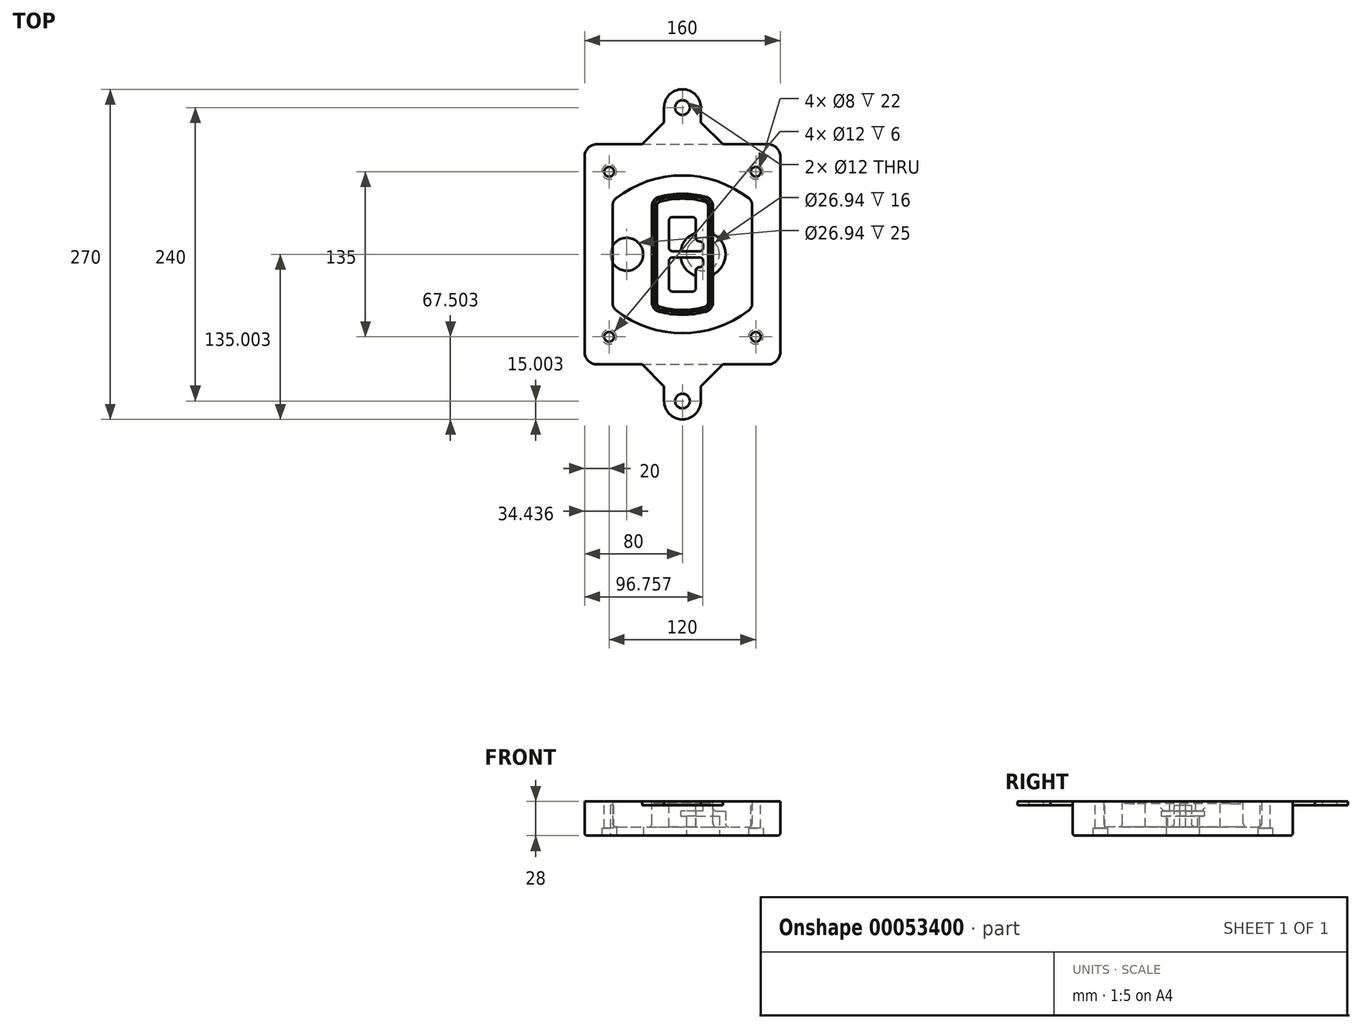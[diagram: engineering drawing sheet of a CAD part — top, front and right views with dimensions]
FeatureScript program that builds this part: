
annotation { "Feature Type Name" : "Feature", "Feature Type Description" : "" }
export const myFeature = defineFeature(function(context is Context, id is Id, definition is map)
    precondition{}
    {
        {
            var Q0;
            Q0=qCreatedBy(makeId("Top.planeOp"),FACE);
            var sketch = newSketch(context, id + "F0", { "sketchPlane" : qUnion([Q0])});
            skPoint(sketch, "E0.rect.middle", {"position": v(0, 0) * mm});
            skLineSegment(sketch, "E1.bottom", {"start": v(24.05, 28.38) * mm, "end": v(164.05, 28.38) * mm});
            skLineSegment(sketch, "E1.top", {"start": v(24.05, 208.38) * mm, "end": v(164.05, 208.38) * mm});
            skLineSegment(sketch, "E1.left", {"start": v(14.05, 38.38) * mm, "end": v(14.05, 198.38) * mm});
            skLineSegment(sketch, "E1.right", {"start": v(174.05, 38.38) * mm, "end": v(174.05, 198.38) * mm});
            skLineSegment(sketch, "E2", {"start": v(14.05, 208.38) * mm, "end": v(174.05, 28.38) * mm, "construction": true});
            skLineSegment(sketch, "E3", {"start": v(174.05, 208.38) * mm, "end": v(14.05, 28.38) * mm, "construction": true});
            skCircle(sketch, "E4", {"center": v(34.05, 185.88) * mm, "radius": 4 * mm});
            skCircle(sketch, "E5", {"center": v(154.05, 185.88) * mm, "radius": 4 * mm});
            skCircle(sketch, "E6", {"center": v(154.05, 50.88) * mm, "radius": 4 * mm});
            skCircle(sketch, "E7", {"center": v(34.05, 50.88) * mm, "radius": 4 * mm});
            skLineSegment(sketch, "E8", {"start": v(34.05, 185.88) * mm, "end": v(154.05, 185.88) * mm, "construction": true});
            skLineSegment(sketch, "E9", {"start": v(154.05, 185.88) * mm, "end": v(154.05, 50.88) * mm, "construction": true});
            skLineSegment(sketch, "E10", {"start": v(154.05, 50.88) * mm, "end": v(34.05, 50.88) * mm, "construction": true});
            skLineSegment(sketch, "E11", {"start": v(34.05, 50.88) * mm, "end": v(34.05, 185.88) * mm, "construction": true});
            skLineSegment(sketch, "E12", {"start": v(34.05, 158.68) * mm, "end": v(34.05, 78.09) * mm});
            skLineSegment(sketch, "E13", {"start": v(154.05, 158.68) * mm, "end": v(154.05, 78.09) * mm});
            skArc(sketch, "E14", {"start": v(150.2, 166.56) * mm, "mid": v(94.05, 185.88) * mm, "end": v(37.9, 166.56) * mm});
            skArc(sketch, "E15", {"start": v(37.9, 70.2) * mm, "mid": v(94.05, 50.88) * mm, "end": v(150.2, 70.2) * mm});
            skLineSegment(sketch, "E16", {"start": v(34.05, 118.38) * mm, "end": v(154.05, 118.38) * mm, "construction": true});
            skPoint(sketch, "E17.visualSharp", {"position": v(34.05, 73.38) * mm});
            skArc(sketch, "E17.filletArc", {"start": v(34.05, 78.09) * mm, "mid": v(35.06, 73.7) * mm, "end": v(37.9, 70.2) * mm});
            skPoint(sketch, "E18.visualSharp", {"position": v(34.05, 163.38) * mm});
            skArc(sketch, "E18.filletArc", {"start": v(37.9, 166.56) * mm, "mid": v(35.06, 163.06) * mm, "end": v(34.05, 158.68) * mm});
            skPoint(sketch, "E19.visualSharp", {"position": v(154.05, 163.38) * mm});
            skArc(sketch, "E19.filletArc", {"start": v(154.05, 158.68) * mm, "mid": v(153.04, 163.06) * mm, "end": v(150.2, 166.56) * mm});
            skPoint(sketch, "E20.visualSharp", {"position": v(154.05, 73.38) * mm});
            skArc(sketch, "E20.filletArc", {"start": v(150.2, 70.2) * mm, "mid": v(153.04, 73.7) * mm, "end": v(154.05, 78.09) * mm});
            skPoint(sketch, "E21.visualSharp", {"position": v(14.05, 208.38) * mm});
            skArc(sketch, "E21.filletArc", {"start": v(24.05, 208.38) * mm, "mid": v(16.98, 205.45) * mm, "end": v(14.05, 198.38) * mm});
            skPoint(sketch, "E22.visualSharp", {"position": v(174.05, 208.38) * mm});
            skArc(sketch, "E22.filletArc", {"start": v(174.05, 198.38) * mm, "mid": v(171.12, 205.45) * mm, "end": v(164.05, 208.38) * mm});
            skPoint(sketch, "E23.visualSharp", {"position": v(174.05, 28.38) * mm});
            skArc(sketch, "E23.filletArc", {"start": v(164.05, 28.38) * mm, "mid": v(171.12, 31.31) * mm, "end": v(174.05, 38.38) * mm});
            skPoint(sketch, "E24.visualSharp", {"position": v(14.05, 28.38) * mm});
            skArc(sketch, "E24.filletArc", {"start": v(14.05, 38.38) * mm, "mid": v(16.98, 31.31) * mm, "end": v(24.05, 28.38) * mm});
            skArc(sketch, "E25.0", {"start": v(151.05, 158.68) * mm, "mid": v(150.34, 161.75) * mm, "end": v(148.36, 164.2) * mm});
            skLineSegment(sketch, "E25.1", {"start": v(151.05, 158.68) * mm, "end": v(151.05, 78.09) * mm});
            skArc(sketch, "E25.2", {"start": v(148.36, 72.57) * mm, "mid": v(150.34, 75.02) * mm, "end": v(151.05, 78.09) * mm});
            skArc(sketch, "E25.3", {"start": v(39.74, 72.57) * mm, "mid": v(94.05, 53.88) * mm, "end": v(148.36, 72.57) * mm});
            skArc(sketch, "E25.4", {"start": v(37.05, 78.09) * mm, "mid": v(37.76, 75.02) * mm, "end": v(39.74, 72.57) * mm});
            skArc(sketch, "E25.5", {"start": v(148.36, 164.2) * mm, "mid": v(94.05, 182.88) * mm, "end": v(39.74, 164.2) * mm});
            skLineSegment(sketch, "E25.6", {"start": v(37.05, 158.68) * mm, "end": v(37.05, 78.09) * mm});
            skArc(sketch, "E25.7", {"start": v(39.74, 164.2) * mm, "mid": v(37.76, 161.75) * mm, "end": v(37.05, 158.68) * mm});
            skArc(sketch, "E26.0", {"start": v(35.43, 169.71) * mm, "mid": v(31.47, 164.82) * mm, "end": v(30.05, 158.68) * mm});
            skArc(sketch, "E26.1", {"start": v(152.67, 169.71) * mm, "mid": v(94.05, 189.88) * mm, "end": v(35.43, 169.71) * mm});
            skArc(sketch, "E26.2", {"start": v(158.05, 158.68) * mm, "mid": v(156.63, 164.82) * mm, "end": v(152.67, 169.71) * mm});
            skLineSegment(sketch, "E26.3", {"start": v(158.05, 158.68) * mm, "end": v(158.05, 78.09) * mm});
            skArc(sketch, "E26.4", {"start": v(152.67, 67.05) * mm, "mid": v(156.63, 71.95) * mm, "end": v(158.05, 78.09) * mm});
            skLineSegment(sketch, "E26.5", {"start": v(30.05, 158.68) * mm, "end": v(30.05, 78.09) * mm});
            skArc(sketch, "E26.6", {"start": v(35.43, 67.05) * mm, "mid": v(94.05, 46.88) * mm, "end": v(152.67, 67.05) * mm});
            skArc(sketch, "E26.7", {"start": v(30.05, 78.09) * mm, "mid": v(31.47, 71.95) * mm, "end": v(35.43, 67.05) * mm});
            skSolve(sketch);
        }
        {
            var Q0;
            Q0=makeQuery(id+"F0.imprint","IMPRINT",FACE,{"disambiguationData":[TD([[makeQuery(id+"F0.imprint","IMPRINT",EDGE,{"derivedFrom":sQuery(id+"F0.wireOp",EDGE,"E1.bottom")}),1.0]])]});
            var Q1;
            Q1=makeQuery(id+"F0.imprint","IMPRINT",FACE,{"disambiguationData":[TD([[makeQuery(id+"F0.imprint","IMPRINT",EDGE,{"derivedFrom":sQuery(id+"F0.wireOp",EDGE,"E12")}),1.0]])]});
            var Q2;
            Q2=makeQuery(id+"F0.imprint","IMPRINT",FACE,{"disambiguationData":[TD([[makeQuery(id+"F0.imprint","IMPRINT",EDGE,{"derivedFrom":sQuery(id+"F0.wireOp",EDGE,"E25.0")}),1.0]])]});
            var Q3;
            Q3=makeQuery(id+"F0.imprint","IMPRINT",FACE,{"disambiguationData":[TD([[makeQuery(id+"F0.imprint","IMPRINT",EDGE,{"derivedFrom":sQuery(id+"F0.wireOp",EDGE,"E12")}),-1.0]])]});
            extrude(context, id + "F1", {"entities" : qUnion([Q0, Q1, Q2, Q3]), "oppositeDirection" : true, "depth" : 25 * mm});
        }
        {
            var Q0;
            Q0=makeQuery(id+"F0.imprint","IMPRINT",FACE,{"disambiguationData":[TD([[makeQuery(id+"F0.imprint","IMPRINT",EDGE,{"derivedFrom":sQuery(id+"F0.wireOp",EDGE,"E12")}),1.0]])]});
            extrude(context, id + "F2", {"entities" : qUnion([Q0]), "operationType" : NewBodyOperationType.ADD, "depth" : 3 * mm});
        }
        {
            var Q0;
            Q0=makeQuery(id+"F0.imprint","IMPRINT",FACE,{"disambiguationData":[TD([[makeQuery(id+"F0.imprint","IMPRINT",EDGE,{"derivedFrom":sQuery(id+"F0.wireOp",EDGE,"E25.0")}),1.0]])]});
            extrude(context, id + "F3", {"entities" : qUnion([Q0]), "operationType" : NewBodyOperationType.REMOVE, "oppositeDirection" : true, "depth" : 18 * mm});
        }
        {
            var Q0;
            Q0=makeQuery(id+"F2.opExtrude","CAP_FACE",FACE,{"disambiguationData":[OSD([sQuery(id+"F0.wireOp",EDGE,"E12"),sQuery(id+"F0.wireOp",EDGE,"E13"),sQuery(id+"F0.wireOp",EDGE,"E14"),sQuery(id+"F0.wireOp",EDGE,"E15"),sQuery(id+"F0.wireOp",EDGE,"E17.filletArc"),sQuery(id+"F0.wireOp",EDGE,"E18.filletArc"),sQuery(id+"F0.wireOp",EDGE,"E19.filletArc"),sQuery(id+"F0.wireOp",EDGE,"E20.filletArc"),sQuery(id+"F0.wireOp",EDGE,"E25.0"),sQuery(id+"F0.wireOp",EDGE,"E25.1"),sQuery(id+"F0.wireOp",EDGE,"E25.2"),sQuery(id+"F0.wireOp",EDGE,"E25.3"),sQuery(id+"F0.wireOp",EDGE,"E25.4"),sQuery(id+"F0.wireOp",EDGE,"E25.5"),sQuery(id+"F0.wireOp",EDGE,"E25.6"),sQuery(id+"F0.wireOp",EDGE,"E25.7")])],"isStart":false});
            var sketch = newSketch(context, id + "F4", { "sketchPlane" : qUnion([Q0])});
            skArc(sketch, "E27.0", {"start": v(74.97, 71.41) * mm, "mid": v(94.05, 68.88) * mm, "end": v(113.13, 71.41) * mm});
            skArc(sketch, "E28.0", {"start": v(113.13, 165.35) * mm, "mid": v(94.05, 167.88) * mm, "end": v(74.97, 165.35) * mm});
            skLineSegment(sketch, "E29", {"start": v(69.05, 157.63) * mm, "end": v(69.05, 79.14) * mm});
            skLineSegment(sketch, "E30", {"start": v(119.05, 157.63) * mm, "end": v(119.05, 79.14) * mm});
            skLineSegment(sketch, "E31", {"start": v(69.05, 163.48) * mm, "end": v(119.05, 163.48) * mm, "construction": true});
            skLineSegment(sketch, "E32", {"start": v(69.05, 73.28) * mm, "end": v(119.05, 73.28) * mm, "construction": true});
            skPoint(sketch, "E33.visualSharp", {"position": v(69.05, 163.48) * mm});
            skArc(sketch, "E33.filletArc", {"start": v(74.97, 165.35) * mm, "mid": v(70.7, 162.5) * mm, "end": v(69.05, 157.63) * mm});
            skPoint(sketch, "E34.visualSharp", {"position": v(119.05, 163.48) * mm});
            skArc(sketch, "E34.filletArc", {"start": v(119.05, 157.63) * mm, "mid": v(117.4, 162.5) * mm, "end": v(113.13, 165.35) * mm});
            skPoint(sketch, "E35.visualSharp", {"position": v(119.05, 73.28) * mm});
            skArc(sketch, "E35.filletArc", {"start": v(113.13, 71.41) * mm, "mid": v(117.4, 74.27) * mm, "end": v(119.05, 79.14) * mm});
            skPoint(sketch, "E36.visualSharp", {"position": v(69.05, 73.28) * mm});
            skArc(sketch, "E36.filletArc", {"start": v(69.05, 79.14) * mm, "mid": v(70.7, 74.27) * mm, "end": v(74.97, 71.41) * mm});
            skArc(sketch, "E37.0", {"start": v(148.36, 164.2) * mm, "mid": v(94.05, 182.88) * mm, "end": v(39.74, 164.2) * mm});
            skArc(sketch, "E37.1", {"start": v(39.74, 164.2) * mm, "mid": v(37.76, 161.75) * mm, "end": v(37.05, 158.68) * mm});
            skLineSegment(sketch, "E37.2", {"start": v(37.05, 158.68) * mm, "end": v(37.05, 78.09) * mm});
            skArc(sketch, "E37.3", {"start": v(37.05, 78.09) * mm, "mid": v(37.76, 75.02) * mm, "end": v(39.74, 72.57) * mm});
            skArc(sketch, "E37.4", {"start": v(39.74, 72.57) * mm, "mid": v(94.05, 53.88) * mm, "end": v(148.36, 72.57) * mm});
            skArc(sketch, "E37.5", {"start": v(148.36, 72.57) * mm, "mid": v(150.34, 75.02) * mm, "end": v(151.05, 78.09) * mm});
            skLineSegment(sketch, "E37.6", {"start": v(151.05, 158.68) * mm, "end": v(151.05, 78.09) * mm});
            skArc(sketch, "E37.7", {"start": v(151.05, 158.68) * mm, "mid": v(150.34, 161.75) * mm, "end": v(148.36, 164.2) * mm});
            skLineSegment(sketch, "E38.0", {"start": v(117.05, 157.63) * mm, "end": v(117.05, 79.14) * mm});
            skArc(sketch, "E38.1", {"start": v(112.61, 73.34) * mm, "mid": v(115.81, 75.49) * mm, "end": v(117.05, 79.14) * mm});
            skArc(sketch, "E38.2", {"start": v(75.49, 73.34) * mm, "mid": v(94.05, 70.88) * mm, "end": v(112.61, 73.34) * mm});
            skArc(sketch, "E38.3", {"start": v(71.05, 79.14) * mm, "mid": v(72.29, 75.49) * mm, "end": v(75.49, 73.34) * mm});
            skLineSegment(sketch, "E38.4", {"start": v(71.05, 157.63) * mm, "end": v(71.05, 79.14) * mm});
            skArc(sketch, "E38.5", {"start": v(117.05, 157.63) * mm, "mid": v(115.81, 161.28) * mm, "end": v(112.61, 163.42) * mm});
            skArc(sketch, "E38.6", {"start": v(75.49, 163.42) * mm, "mid": v(72.29, 161.28) * mm, "end": v(71.05, 157.63) * mm});
            skArc(sketch, "E38.7", {"start": v(112.61, 163.42) * mm, "mid": v(94.05, 165.88) * mm, "end": v(75.49, 163.42) * mm});
            skArc(sketch, "E39.0", {"start": v(115.05, 157.63) * mm, "mid": v(114.23, 160.06) * mm, "end": v(112.1, 161.5) * mm});
            skLineSegment(sketch, "E39.1", {"start": v(115.05, 157.63) * mm, "end": v(115.05, 79.14) * mm});
            skArc(sketch, "E39.2", {"start": v(112.1, 75.27) * mm, "mid": v(114.23, 76.7) * mm, "end": v(115.05, 79.14) * mm});
            skArc(sketch, "E39.3", {"start": v(76, 75.27) * mm, "mid": v(94.05, 72.88) * mm, "end": v(112.1, 75.27) * mm});
            skArc(sketch, "E39.4", {"start": v(73.05, 79.14) * mm, "mid": v(73.87, 76.7) * mm, "end": v(76, 75.27) * mm});
            skArc(sketch, "E39.5", {"start": v(112.1, 161.5) * mm, "mid": v(94.05, 163.88) * mm, "end": v(76, 161.5) * mm});
            skLineSegment(sketch, "E39.6", {"start": v(73.05, 157.63) * mm, "end": v(73.05, 79.14) * mm});
            skArc(sketch, "E39.7", {"start": v(76, 161.5) * mm, "mid": v(73.87, 160.06) * mm, "end": v(73.05, 157.63) * mm});
            skLineSegment(sketch, "E40", {"start": v(69.05, 118.38) * mm, "end": v(119.05, 118.38) * mm, "construction": true});
            skLineSegment(sketch, "E41", {"start": v(83.05, 123.88) * mm, "end": v(83.05, 145.88) * mm});
            skLineSegment(sketch, "E42", {"start": v(86.05, 148.88) * mm, "end": v(102.05, 148.88) * mm});
            skLineSegment(sketch, "E43", {"start": v(105.05, 145.88) * mm, "end": v(105.05, 131.88) * mm});
            skLineSegment(sketch, "E44", {"start": v(108.05, 128.88) * mm, "end": v(108.05, 128.88) * mm});
            skLineSegment(sketch, "E45", {"start": v(111.05, 125.88) * mm, "end": v(111.05, 123.88) * mm});
            skLineSegment(sketch, "E46", {"start": v(108.05, 120.88) * mm, "end": v(86.05, 120.88) * mm});
            skPoint(sketch, "E47.visualSharp", {"position": v(83.05, 148.88) * mm});
            skArc(sketch, "E47.filletArc", {"start": v(86.05, 148.88) * mm, "mid": v(83.93, 148) * mm, "end": v(83.05, 145.88) * mm});
            skPoint(sketch, "E48.visualSharp", {"position": v(105.05, 148.88) * mm});
            skArc(sketch, "E48.filletArc", {"start": v(105.05, 145.88) * mm, "mid": v(104.17, 148) * mm, "end": v(102.05, 148.88) * mm});
            skPoint(sketch, "E49.visualSharp", {"position": v(105.05, 128.88) * mm});
            skArc(sketch, "E49.filletArc", {"start": v(105.05, 131.88) * mm, "mid": v(105.93, 129.76) * mm, "end": v(108.05, 128.88) * mm});
            skPoint(sketch, "E50.visualSharp", {"position": v(111.05, 128.88) * mm});
            skArc(sketch, "E50.filletArc", {"start": v(111.05, 125.88) * mm, "mid": v(110.17, 128) * mm, "end": v(108.05, 128.88) * mm});
            skPoint(sketch, "E51.visualSharp", {"position": v(111.05, 120.88) * mm});
            skArc(sketch, "E51.filletArc", {"start": v(108.05, 120.88) * mm, "mid": v(110.17, 121.76) * mm, "end": v(111.05, 123.88) * mm});
            skPoint(sketch, "E52.visualSharp", {"position": v(83.05, 120.88) * mm});
            skArc(sketch, "E52.filletArc", {"start": v(83.05, 123.88) * mm, "mid": v(83.93, 121.76) * mm, "end": v(86.05, 120.88) * mm});
            skLineSegment(sketch, "E53.0.MirrorCS", {"start": v(108.05, 115.88) * mm, "end": v(86.05, 115.88) * mm});
            skArc(sketch, "E54.0.MirrorCS", {"start": v(83.05, 112.88) * mm, "mid": v(83.93, 115) * mm, "end": v(86.05, 115.88) * mm});
            skLineSegment(sketch, "E55.0.MirrorCS", {"start": v(83.05, 112.88) * mm, "end": v(83.05, 90.88) * mm});
            skArc(sketch, "E56.0.MirrorCS", {"start": v(86.05, 87.88) * mm, "mid": v(83.93, 88.76) * mm, "end": v(83.05, 90.88) * mm});
            skLineSegment(sketch, "E57.0.MirrorCS", {"start": v(86.05, 87.88) * mm, "end": v(102.05, 87.88) * mm});
            skArc(sketch, "E58.0.MirrorCS", {"start": v(105.05, 90.88) * mm, "mid": v(104.17, 88.76) * mm, "end": v(102.05, 87.88) * mm});
            skLineSegment(sketch, "E59.0.MirrorCS", {"start": v(105.05, 90.88) * mm, "end": v(105.05, 104.88) * mm});
            skArc(sketch, "E60.0.MirrorCS", {"start": v(105.05, 104.88) * mm, "mid": v(105.93, 107) * mm, "end": v(108.05, 107.88) * mm});
            skArc(sketch, "E61.0.MirrorCS", {"start": v(111.05, 110.88) * mm, "mid": v(110.17, 108.76) * mm, "end": v(108.05, 107.88) * mm});
            skLineSegment(sketch, "E62.0.MirrorCS", {"start": v(111.05, 110.88) * mm, "end": v(111.05, 112.88) * mm});
            skArc(sketch, "E63.0.MirrorCS", {"start": v(108.05, 115.88) * mm, "mid": v(110.17, 115) * mm, "end": v(111.05, 112.88) * mm});
            skSolve(sketch);
        }
        {
            var Q0;
            Q0=makeQuery(id+"F4.imprint","IMPRINT",FACE,{"disambiguationData":[TD([[makeQuery(id+"F4.imprint","IMPRINT",EDGE,{"derivedFrom":sQuery(id+"F4.wireOp",EDGE,"E27.0")}),1.0]])]});
            var Q1;
            Q1=makeQuery(id+"F4.imprint","IMPRINT",FACE,{"disambiguationData":[TD([[makeQuery(id+"F4.imprint","IMPRINT",EDGE,{"derivedFrom":sQuery(id+"F4.wireOp",EDGE,"E38.0")}),-1.0]])]});
            var Q2;
            Q2=makeQuery(id+"F4.imprint","IMPRINT",FACE,{"disambiguationData":[TD([[makeQuery(id+"F4.imprint","IMPRINT",EDGE,{"derivedFrom":sQuery(id+"F4.wireOp",EDGE,"E39.0")}),1.0]])]});
            extrude(context, id + "F5", {"entities" : qUnion([Q0, Q1, Q2]), "operationType" : NewBodyOperationType.ADD, "endBound" : BoundingType.UP_TO_NEXT, "oppositeDirection" : true, "depth" : 25 * mm});
        }
        {
            var Q0;
            Q0=makeQuery(id+"F4.imprint","IMPRINT",FACE,{"disambiguationData":[TD([[makeQuery(id+"F4.imprint","IMPRINT",EDGE,{"derivedFrom":sQuery(id+"F4.wireOp",EDGE,"E38.0")}),-1.0]])]});
            extrude(context, id + "F6", {"entities" : qUnion([Q0]), "operationType" : NewBodyOperationType.REMOVE, "oppositeDirection" : true, "depth" : 2 * mm});
        }
        {
            var Q0;
            Q0=makeQuery(id+"F1.opExtrude","CAP_FACE",FACE,{"disambiguationData":[OSD([sQuery(id+"F0.wireOp",EDGE,"E1.bottom"),sQuery(id+"F0.wireOp",EDGE,"E1.top"),sQuery(id+"F0.wireOp",EDGE,"E1.left"),sQuery(id+"F0.wireOp",EDGE,"E1.right"),sQuery(id+"F0.wireOp",EDGE,"E4"),sQuery(id+"F0.wireOp",EDGE,"E5"),sQuery(id+"F0.wireOp",EDGE,"E6"),sQuery(id+"F0.wireOp",EDGE,"E7"),sQuery(id+"F0.wireOp",EDGE,"E21.filletArc"),sQuery(id+"F0.wireOp",EDGE,"E22.filletArc"),sQuery(id+"F0.wireOp",EDGE,"E23.filletArc"),sQuery(id+"F0.wireOp",EDGE,"E24.filletArc")])],"isStart":false});
            var sketch = newSketch(context, id + "F7", { "sketchPlane" : qUnion([Q0])});
            skCircle(sketch, "E64", {"center": v(110.8, -118.38) * mm, "radius": 13.47 * mm});
            skCircle(sketch, "E65", {"center": v(48.49, -118.38) * mm, "radius": 13.47 * mm});
            skLineSegment(sketch, "E66", {"start": v(174.05, -118.38) * mm, "end": v(14.05, -118.38) * mm});
            skCircle(sketch, "E67", {"center": v(110.8, -118.38) * mm, "radius": 18.47 * mm});
            skCircle(sketch, "E68", {"center": v(154.05, -185.88) * mm, "radius": 6 * mm});
            skCircle(sketch, "E69", {"center": v(34.05, -185.88) * mm, "radius": 6 * mm});
            skCircle(sketch, "E70", {"center": v(34.05, -50.88) * mm, "radius": 6 * mm});
            skCircle(sketch, "E71", {"center": v(154.05, -50.88) * mm, "radius": 6 * mm});
            skSolve(sketch);
        }
        {
            var Q0;
            {var subQ1=sQuery(id+"F7.wireOp",EDGE,"E66");var subQ4=sQuery(id+"F7.wireOp",EDGE,"E64");var subQ6=makeQuery(id+"F7.imprint","INTERSECT",VERTEX,{"disambiguationData":[OD(0.0)],"derivedFrom":[subQ4,subQ1]});Q0=makeQuery(id+"F7.imprint","IMPRINT",FACE,{"disambiguationData":[TD([[makeQuery(id+"F7.imprint","IMPRINT",EDGE,{"disambiguationData":[TD([[subQ6,-1.0]])],"derivedFrom":subQ4}),-1.0]])]});}
            var Q1;
            {var subQ0=sQuery(id+"F7.wireOp",EDGE,"E66");var subQ1=sQuery(id+"F7.wireOp",EDGE,"E64");var subQ3=makeQuery(id+"F7.imprint","INTERSECT",VERTEX,{"disambiguationData":[OD(0.0)],"derivedFrom":[subQ1,subQ0]});Q1=makeQuery(id+"F7.imprint","IMPRINT",FACE,{"disambiguationData":[TD([[makeQuery(id+"F7.imprint","IMPRINT",EDGE,{"disambiguationData":[TD([[subQ3,-1.0]])],"derivedFrom":subQ1}),1.0]])]});}
            var Q2;
            {var subQ0=sQuery(id+"F7.wireOp",EDGE,"E66");var subQ1=sQuery(id+"F7.wireOp",EDGE,"E64");var subQ3=makeQuery(id+"F7.imprint","INTERSECT",VERTEX,{"disambiguationData":[OD(0.0)],"derivedFrom":[subQ1,subQ0]});Q2=makeQuery(id+"F7.imprint","IMPRINT",FACE,{"disambiguationData":[TD([[makeQuery(id+"F7.imprint","IMPRINT",EDGE,{"disambiguationData":[TD([[subQ3,1.0]])],"derivedFrom":subQ1}),1.0]])]});}
            var Q3;
            {var subQ1=sQuery(id+"F7.wireOp",EDGE,"E66");var subQ4=sQuery(id+"F7.wireOp",EDGE,"E64");var subQ6=makeQuery(id+"F7.imprint","INTERSECT",VERTEX,{"disambiguationData":[OD(0.0)],"derivedFrom":[subQ4,subQ1]});Q3=makeQuery(id+"F7.imprint","IMPRINT",FACE,{"disambiguationData":[TD([[makeQuery(id+"F7.imprint","IMPRINT",EDGE,{"disambiguationData":[TD([[subQ6,1.0]])],"derivedFrom":subQ4}),-1.0]])]});}
            extrude(context, id + "F8", {"entities" : qUnion([Q0, Q1, Q2, Q3]), "operationType" : NewBodyOperationType.ADD, "oppositeDirection" : true, "depth" : 20 * mm});
        }
        {
            var Q0;
            {var subQ0=sQuery(id+"F7.wireOp",EDGE,"E66");var subQ1=sQuery(id+"F7.wireOp",EDGE,"E64");var subQ3=makeQuery(id+"F7.imprint","INTERSECT",VERTEX,{"disambiguationData":[OD(0.0)],"derivedFrom":[subQ1,subQ0]});Q0=makeQuery(id+"F7.imprint","IMPRINT",FACE,{"disambiguationData":[TD([[makeQuery(id+"F7.imprint","IMPRINT",EDGE,{"disambiguationData":[TD([[subQ3,-1.0]])],"derivedFrom":subQ1}),1.0]])]});}
            var Q1;
            {var subQ0=sQuery(id+"F7.wireOp",EDGE,"E66");var subQ1=sQuery(id+"F7.wireOp",EDGE,"E64");var subQ3=makeQuery(id+"F7.imprint","INTERSECT",VERTEX,{"disambiguationData":[OD(0.0)],"derivedFrom":[subQ1,subQ0]});Q1=makeQuery(id+"F7.imprint","IMPRINT",FACE,{"disambiguationData":[TD([[makeQuery(id+"F7.imprint","IMPRINT",EDGE,{"disambiguationData":[TD([[subQ3,1.0]])],"derivedFrom":subQ1}),1.0]])]});}
            extrude(context, id + "F9", {"entities" : qUnion([Q0, Q1]), "operationType" : NewBodyOperationType.REMOVE, "oppositeDirection" : true, "depth" : 16 * mm});
        }
        {
            var Q0;
            {var subQ0=sQuery(id+"F7.wireOp",EDGE,"E66");var subQ1=sQuery(id+"F7.wireOp",EDGE,"E65");var subQ3=makeQuery(id+"F7.imprint","INTERSECT",VERTEX,{"disambiguationData":[OD(0.0)],"derivedFrom":[subQ1,subQ0]});Q0=makeQuery(id+"F7.imprint","IMPRINT",FACE,{"disambiguationData":[TD([[makeQuery(id+"F7.imprint","IMPRINT",EDGE,{"disambiguationData":[TD([[subQ3,-1.0]])],"derivedFrom":subQ1}),1.0]])]});}
            var Q1;
            {var subQ0=sQuery(id+"F7.wireOp",EDGE,"E66");var subQ1=sQuery(id+"F7.wireOp",EDGE,"E65");var subQ3=makeQuery(id+"F7.imprint","INTERSECT",VERTEX,{"disambiguationData":[OD(0.0)],"derivedFrom":[subQ1,subQ0]});Q1=makeQuery(id+"F7.imprint","IMPRINT",FACE,{"disambiguationData":[TD([[makeQuery(id+"F7.imprint","IMPRINT",EDGE,{"disambiguationData":[TD([[subQ3,1.0]])],"derivedFrom":subQ1}),1.0]])]});}
            extrude(context, id + "F10", {"entities" : qUnion([Q0, Q1]), "operationType" : NewBodyOperationType.REMOVE, "oppositeDirection" : true, "depth" : 25 * mm});
        }
        {
            var Q0;
            Q0=makeQuery(id+"F7.imprint","IMPRINT",FACE,{"disambiguationData":[TD([[makeQuery(id+"F7.imprint","IMPRINT",EDGE,{"derivedFrom":sQuery(id+"F7.wireOp",EDGE,"E68")}),1.0]])]});
            var Q1;
            Q1=makeQuery(id+"F7.imprint","IMPRINT",FACE,{"disambiguationData":[TD([[makeQuery(id+"F7.imprint","IMPRINT",EDGE,{"derivedFrom":makeQuery(id+"F1.opExtrude","CAP_EDGE",EDGE,{"disambiguationData":[OSD([sQuery(id+"F0.wireOp",EDGE,"E5")])],"isStart":false})}),-1.0]])]});
            var Q2;
            Q2=makeQuery(id+"F7.imprint","IMPRINT",FACE,{"disambiguationData":[TD([[makeQuery(id+"F7.imprint","IMPRINT",EDGE,{"derivedFrom":sQuery(id+"F7.wireOp",EDGE,"E69")}),1.0]])]});
            var Q3;
            Q3=makeQuery(id+"F7.imprint","IMPRINT",FACE,{"disambiguationData":[TD([[makeQuery(id+"F7.imprint","IMPRINT",EDGE,{"derivedFrom":makeQuery(id+"F1.opExtrude","CAP_EDGE",EDGE,{"disambiguationData":[OSD([sQuery(id+"F0.wireOp",EDGE,"E4")])],"isStart":false})}),-1.0]])]});
            var Q4;
            Q4=makeQuery(id+"F7.imprint","IMPRINT",FACE,{"disambiguationData":[TD([[makeQuery(id+"F7.imprint","IMPRINT",EDGE,{"derivedFrom":sQuery(id+"F7.wireOp",EDGE,"E70")}),1.0]])]});
            var Q5;
            Q5=makeQuery(id+"F7.imprint","IMPRINT",FACE,{"disambiguationData":[TD([[makeQuery(id+"F7.imprint","IMPRINT",EDGE,{"derivedFrom":makeQuery(id+"F1.opExtrude","CAP_EDGE",EDGE,{"disambiguationData":[OSD([sQuery(id+"F0.wireOp",EDGE,"E7")])],"isStart":false})}),-1.0]])]});
            var Q6;
            Q6=makeQuery(id+"F7.imprint","IMPRINT",FACE,{"disambiguationData":[TD([[makeQuery(id+"F7.imprint","IMPRINT",EDGE,{"derivedFrom":sQuery(id+"F7.wireOp",EDGE,"E71")}),1.0]])]});
            var Q7;
            Q7=makeQuery(id+"F7.imprint","IMPRINT",FACE,{"disambiguationData":[TD([[makeQuery(id+"F7.imprint","IMPRINT",EDGE,{"derivedFrom":makeQuery(id+"F1.opExtrude","CAP_EDGE",EDGE,{"disambiguationData":[OSD([sQuery(id+"F0.wireOp",EDGE,"E6")])],"isStart":false})}),-1.0]])]});
            extrude(context, id + "F11", {"entities" : qUnion([Q0, Q1, Q2, Q3, Q4, Q5, Q6, Q7]), "operationType" : NewBodyOperationType.REMOVE, "oppositeDirection" : true, "depth" : 6 * mm});
        }
        {
            var Q0;
            Q0=makeQuery(id+"F9.boolean.opBoolean","COPY",FACE,{"derivedFrom":makeQuery(id+"F9.opExtrude","CAP_FACE",FACE,{"disambiguationData":[OSD([sQuery(id+"F7.wireOp",EDGE,"E64")])],"isStart":false})});
            var sketch = newSketch(context, id + "F12", { "sketchPlane" : qUnion([Q0])});
            skArc(sketch, "E72.0", {"start": v(105.05, -100.83) * mm, "mid": v(96.62, -106.56) * mm, "end": v(92.5, -115.88) * mm});
            skArc(sketch, "E72.1", {"start": v(92.5, -120.88) * mm, "mid": v(96.62, -130.2) * mm, "end": v(105.05, -135.93) * mm});
            skLineSegment(sketch, "E73", {"start": v(92.5, -120.88) * mm, "end": v(108.05, -120.88) * mm});
            skLineSegment(sketch, "E74.0", {"start": v(108.05, -115.88) * mm, "end": v(92.5, -115.88) * mm});
            skArc(sketch, "E74.1", {"start": v(108.05, -115.88) * mm, "mid": v(110.17, -115) * mm, "end": v(111.05, -112.88) * mm});
            skLineSegment(sketch, "E74.2", {"start": v(111.05, -110.88) * mm, "end": v(111.05, -112.88) * mm});
            skArc(sketch, "E74.3", {"start": v(111.05, -110.88) * mm, "mid": v(110.17, -108.76) * mm, "end": v(108.05, -107.88) * mm});
            skArc(sketch, "E74.4", {"start": v(105.05, -104.88) * mm, "mid": v(105.93, -107) * mm, "end": v(108.05, -107.88) * mm});
            skLineSegment(sketch, "E74.5", {"start": v(105.05, -100.83) * mm, "end": v(105.05, -104.88) * mm});
            skLineSegment(sketch, "E74.7", {"start": v(108.05, -120.88) * mm, "end": v(92.5, -120.88) * mm});
            skArc(sketch, "E74.8", {"start": v(108.05, -120.88) * mm, "mid": v(110.17, -121.76) * mm, "end": v(111.05, -123.88) * mm});
            skLineSegment(sketch, "E74.9", {"start": v(111.05, -125.88) * mm, "end": v(111.05, -123.88) * mm});
            skArc(sketch, "E74.10", {"start": v(111.05, -125.88) * mm, "mid": v(110.17, -128) * mm, "end": v(108.05, -128.88) * mm});
            skArc(sketch, "E74.11", {"start": v(105.05, -131.88) * mm, "mid": v(105.93, -129.76) * mm, "end": v(108.05, -128.88) * mm});
            skLineSegment(sketch, "E74.12", {"start": v(105.05, -135.93) * mm, "end": v(105.05, -131.88) * mm});
            skPoint(sketch, "E75.orphan", {"position": v(105.05, -145.88) * mm});
            skPoint(sketch, "E76.orphan", {"position": v(86.05, -120.88) * mm});
            skPoint(sketch, "E77.orphan", {"position": v(86.05, -115.88) * mm});
            skPoint(sketch, "E78.orphan", {"position": v(105.05, -90.88) * mm});
            skSolve(sketch);
        }
        {
            var Q0;
            {var subQ7=sQuery(id+"F12.wireOp",EDGE,"E72.0");var subQ14=sQuery(id+"F12.wireOp",EDGE,"E72.1");var subQ16=sQuery(id+"F12.wireOp",EDGE,"E74.1");var subQ18=sQuery(id+"F12.wireOp",EDGE,"E74.8");Q0=qUnion([makeQuery(id+"F12.imprint","IMPRINT",FACE,{"disambiguationData":[TD([[makeQuery(id+"F12.imprint","IMPRINT",EDGE,{"derivedFrom":subQ7}),1.0]])]}),makeQuery(id+"F12.imprint","IMPRINT",FACE,{"disambiguationData":[TD([[makeQuery(id+"F12.imprint","IMPRINT",EDGE,{"derivedFrom":subQ14}),1.0]])]}),makeQuery(id+"F12.imprint","IMPRINT",FACE,{"disambiguationData":[TD([[makeQuery(id+"F12.imprint","IMPRINT",EDGE,{"derivedFrom":subQ16}),1.0]])]}),makeQuery(id+"F12.imprint","IMPRINT",FACE,{"disambiguationData":[TD([[makeQuery(id+"F12.imprint","IMPRINT",EDGE,{"derivedFrom":subQ18}),-1.0]])]})]);}
            var Q1;
            Q1=makeQuery(id+"F5.boolean.opBoolean","SPLIT",FACE,{"disambiguationData":[TD([makeQuery(id+"F5.opExtrude","SWEPT_FACE",FACE,{"disambiguationData":[OSD([sQuery(id+"F4.wireOp",EDGE,"E41")])]})])],"derivedFrom":makeQuery(id+"F3.boolean.opBoolean","COPY",FACE,{"derivedFrom":makeQuery(id+"F3.opExtrude","CAP_FACE",FACE,{"disambiguationData":[OSD([sQuery(id+"F0.wireOp",EDGE,"E25.0"),sQuery(id+"F0.wireOp",EDGE,"E25.1"),sQuery(id+"F0.wireOp",EDGE,"E25.2"),sQuery(id+"F0.wireOp",EDGE,"E25.3"),sQuery(id+"F0.wireOp",EDGE,"E25.4"),sQuery(id+"F0.wireOp",EDGE,"E25.5"),sQuery(id+"F0.wireOp",EDGE,"E25.6"),sQuery(id+"F0.wireOp",EDGE,"E25.7")])],"isStart":false})})});
            extrude(context, id + "F13", {"entities" : qUnion([Q0]), "operationType" : NewBodyOperationType.REMOVE, "endBound" : BoundingType.UP_TO_SURFACE, "endBoundEntityFace" : qUnion([Q1]), "depth" : 25 * mm});
        }
        {
            var Q0;
            Q0=makeQuery(id+"F3.boolean.opBoolean","COPY",EDGE,{"derivedFrom":makeQuery(id+"F3.opExtrude","CAP_EDGE",EDGE,{"disambiguationData":[OSD([sQuery(id+"F0.wireOp",EDGE,"E25.6")])],"isStart":false})});
            var Q1;
            Q1=makeQuery(id+"F8.boolean.opBoolean","INTERSECT",EDGE,{"derivedFrom":[makeQuery(id+"F5.opExtrude","SWEPT_FACE",FACE,{"disambiguationData":[OSD([sQuery(id+"F4.wireOp",EDGE,"E30")])]}),makeQuery(id+"F8.opExtrude","CAP_FACE",FACE,{"disambiguationData":[OSD([sQuery(id+"F7.wireOp",EDGE,"E67")])],"isStart":false})]});
            var Q2;
            Q2=makeQuery(id+"F8.boolean.opBoolean","INTERSECT",EDGE,{"disambiguationData":[OD(1.0)],"derivedFrom":[makeQuery(id+"F5.opExtrude","SWEPT_FACE",FACE,{"disambiguationData":[OSD([sQuery(id+"F4.wireOp",EDGE,"E30")])]}),makeQuery(id+"F8.opExtrude","SWEPT_FACE",FACE,{"disambiguationData":[OSD([sQuery(id+"F7.wireOp",EDGE,"E67")])]})]});
            var Q3;
            {var subQ0=sQuery(id+"F4.wireOp",EDGE,"E30");Q3=makeQuery(id+"F8.boolean.opBoolean","SPLIT",EDGE,{"disambiguationData":[TD([makeQuery(id+"F5.opExtrude","SWEPT_FACE",FACE,{"disambiguationData":[OSD([sQuery(id+"F4.wireOp",EDGE,"E35.filletArc")])]})])],"derivedFrom":makeQuery(id+"F5.opExtrude","CAP_EDGE",EDGE,{"disambiguationData":[OSD([subQ0])],"isStart":false})});}
            var Q4;
            {var subQ0=sQuery(id+"F0.wireOp",EDGE,"E25.7");var subQ1=sQuery(id+"F0.wireOp",EDGE,"E25.1");var subQ2=sQuery(id+"F0.wireOp",EDGE,"E25.6");var subQ3=sQuery(id+"F0.wireOp",EDGE,"E25.5");var subQ4=sQuery(id+"F0.wireOp",EDGE,"E25.4");var subQ5=sQuery(id+"F0.wireOp",EDGE,"E25.0");var subQ6=sQuery(id+"F0.wireOp",EDGE,"E25.2");var subQ7=sQuery(id+"F0.wireOp",EDGE,"E25.3");Q4=makeQuery(id+"F8.boolean.opBoolean","INTERSECT",EDGE,{"derivedFrom":[makeQuery(id+"F5.boolean.opBoolean","SPLIT",FACE,{"disambiguationData":[TD([makeQuery(id+"F2.opExtrude","SWEPT_FACE",FACE,{"disambiguationData":[OSD([subQ5])]})])],"derivedFrom":makeQuery(id+"F3.boolean.opBoolean","COPY",FACE,{"derivedFrom":makeQuery(id+"F3.opExtrude","CAP_FACE",FACE,{"disambiguationData":[OSD([subQ5,subQ1,subQ6,subQ7,subQ4,subQ3,subQ2,subQ0])],"isStart":false})})}),makeQuery(id+"F8.opExtrude","SWEPT_FACE",FACE,{"disambiguationData":[OSD([sQuery(id+"F7.wireOp",EDGE,"E67")])]})]});}
            var Q5;
            Q5=makeQuery(id+"F8.boolean.opBoolean","INTERSECT",EDGE,{"disambiguationData":[OD(0.0)],"derivedFrom":[makeQuery(id+"F5.opExtrude","SWEPT_FACE",FACE,{"disambiguationData":[OSD([sQuery(id+"F4.wireOp",EDGE,"E30")])]}),makeQuery(id+"F8.opExtrude","SWEPT_FACE",FACE,{"disambiguationData":[OSD([sQuery(id+"F7.wireOp",EDGE,"E67")])]})]});
            fillet(context, id + "F14", {"entities" : qUnion([Q0, Q1, Q2, Q3, Q4, Q5]), "radius" : 3 * mm, "tangentPropagation" : true, "allowEdgeOverflow" : false});
        }
        {
            var Q0;
            Q0=makeQuery(id+"F1.opExtrude","CAP_EDGE",EDGE,{"disambiguationData":[OSD([sQuery(id+"F0.wireOp",EDGE,"E1.bottom")])],"isStart":false});
            fillet(context, id + "F15", {"entities" : qUnion([Q0]), "radius" : 2 * mm, "tangentPropagation" : true, "allowEdgeOverflow" : false});
        }
        {
            var Q0;
            {var subQ0=sQuery(id+"F0.wireOp",EDGE,"E1.bottom");var subQ1=sQuery(id+"F0.wireOp",EDGE,"E1.top");var subQ2=sQuery(id+"F0.wireOp",EDGE,"E1.left");var subQ3=sQuery(id+"F0.wireOp",EDGE,"E1.right");var subQ4=sQuery(id+"F0.wireOp",EDGE,"E4");var subQ5=sQuery(id+"F0.wireOp",EDGE,"E5");var subQ6=sQuery(id+"F0.wireOp",EDGE,"E6");var subQ7=sQuery(id+"F0.wireOp",EDGE,"E7");var subQ8=sQuery(id+"F0.wireOp",EDGE,"E21.filletArc");var subQ9=sQuery(id+"F0.wireOp",EDGE,"E22.filletArc");var subQ10=sQuery(id+"F0.wireOp",EDGE,"E23.filletArc");var subQ11=sQuery(id+"F0.wireOp",EDGE,"E24.filletArc");Q0=makeQuery(id+"F2.boolean.opBoolean","SPLIT",FACE,{"disambiguationData":[TD([makeQuery(id+"F1.opExtrude","SWEPT_FACE",FACE,{"disambiguationData":[OSD([subQ0])]})])],"derivedFrom":makeQuery(id+"F1.opExtrude","CAP_FACE",FACE,{"disambiguationData":[OSD([subQ0,subQ1,subQ2,subQ3,subQ4,subQ5,subQ6,subQ7,subQ8,subQ9,subQ10,subQ11])],"isStart":true})});}
            var sketch = newSketch(context, id + "F16", { "sketchPlane" : qUnion([Q0])});
            skSolve(sketch);
        }
        {
            var Q0;
            Q0=makeQuery(id+"F16.imprint","IMPRINT",FACE,{"disambiguationData":[TD([[makeQuery(id+"F16.imprint","IMPRINT",EDGE,{"derivedFrom":makeQuery(id+"F1.opExtrude","CAP_EDGE",EDGE,{"disambiguationData":[OSD([sQuery(id+"F0.wireOp",EDGE,"E1.bottom")])],"isStart":true})}),1.0]])]});
            var sketch = newSketch(context, id + "F17", { "sketchPlane" : qUnion([Q0])});
            skLineSegment(sketch, "E79.0", {"start": v(14.05, 38.38) * mm, "end": v(14.05, 198.38) * mm});
            skArc(sketch, "E80.0", {"start": v(14.05, 38.38) * mm, "mid": v(16.98, 31.31) * mm, "end": v(24.05, 28.38) * mm});
            skLineSegment(sketch, "E81.0", {"start": v(24.05, 28.38) * mm, "end": v(164.05, 28.38) * mm});
            skArc(sketch, "E82.0", {"start": v(164.05, 28.38) * mm, "mid": v(171.12, 31.31) * mm, "end": v(174.05, 38.38) * mm});
            skCircle(sketch, "E83.0", {"center": v(154.05, 50.88) * mm, "radius": 4 * mm});
            skCircle(sketch, "E84.0", {"center": v(34.05, 50.88) * mm, "radius": 4 * mm});
            skLineSegment(sketch, "E85.0", {"start": v(174.05, 38.38) * mm, "end": v(174.05, 198.38) * mm});
            skArc(sketch, "E86.0", {"start": v(174.05, 198.38) * mm, "mid": v(171.12, 205.45) * mm, "end": v(164.05, 208.38) * mm});
            skLineSegment(sketch, "E87.0", {"start": v(24.05, 208.38) * mm, "end": v(164.05, 208.38) * mm});
            skArc(sketch, "E88.0", {"start": v(24.05, 208.38) * mm, "mid": v(16.98, 205.45) * mm, "end": v(14.05, 198.38) * mm});
            skArc(sketch, "E89.0", {"start": v(37.9, 70.2) * mm, "mid": v(94.05, 50.88) * mm, "end": v(150.2, 70.2) * mm});
            skArc(sketch, "E90.0", {"start": v(150.2, 70.2) * mm, "mid": v(153.04, 73.7) * mm, "end": v(154.05, 78.09) * mm});
            skLineSegment(sketch, "E91.0", {"start": v(154.05, 158.68) * mm, "end": v(154.05, 78.09) * mm});
            skArc(sketch, "E92.0", {"start": v(154.05, 158.68) * mm, "mid": v(153.04, 163.06) * mm, "end": v(150.2, 166.56) * mm});
            skCircle(sketch, "E93.0", {"center": v(154.05, 185.88) * mm, "radius": 4 * mm});
            skCircle(sketch, "E94.0", {"center": v(34.05, 185.88) * mm, "radius": 4 * mm});
            skArc(sketch, "E95.0", {"start": v(150.2, 166.56) * mm, "mid": v(94.05, 185.88) * mm, "end": v(37.9, 166.56) * mm});
            skArc(sketch, "E96.0", {"start": v(37.9, 166.56) * mm, "mid": v(35.06, 163.06) * mm, "end": v(34.05, 158.68) * mm});
            skLineSegment(sketch, "E97.0", {"start": v(34.05, 158.68) * mm, "end": v(34.05, 78.09) * mm});
            skArc(sketch, "E98.0", {"start": v(34.05, 78.09) * mm, "mid": v(35.06, 73.7) * mm, "end": v(37.9, 70.2) * mm});
            skLineSegment(sketch, "E99", {"start": v(94.05, 208.38) * mm, "end": v(94.05, 238.38) * mm, "construction": true});
            skCircle(sketch, "E100", {"center": v(94.05, 238.38) * mm, "radius": 6 * mm});
            skArc(sketch, "E101", {"start": v(109.05, 238.38) * mm, "mid": v(94.05, 253.38) * mm, "end": v(79.05, 238.38) * mm});
            skLineSegment(sketch, "E102", {"start": v(79.05, 238.38) * mm, "end": v(79.05, 226.38) * mm});
            skLineSegment(sketch, "E103", {"start": v(79.05, 226.38) * mm, "end": v(61.05, 208.38) * mm});
            skLineSegment(sketch, "E104.MirrorCS", {"start": v(109.05, 226.38) * mm, "end": v(127.05, 208.38) * mm});
            skLineSegment(sketch, "E105.MirrorCS", {"start": v(109.05, 238.38) * mm, "end": v(109.05, 226.38) * mm});
            skLineSegment(sketch, "E106", {"start": v(14.05, 118.38) * mm, "end": v(174.05, 118.38) * mm, "construction": true});
            skArc(sketch, "E107.MirrorCS", {"start": v(109.05, -1.62) * mm, "mid": v(94.05, -16.62) * mm, "end": v(79.05, -1.62) * mm});
            skLineSegment(sketch, "E108.MirrorCS", {"start": v(109.05, -1.62) * mm, "end": v(109.05, 10.38) * mm});
            skLineSegment(sketch, "E109.MirrorCS", {"start": v(79.05, -1.62) * mm, "end": v(79.05, 10.38) * mm});
            skCircle(sketch, "E110.MirrorC", {"center": v(94.05, -1.62) * mm, "radius": 6 * mm});
            skLineSegment(sketch, "E111.MirrorCS", {"start": v(109.05, 10.38) * mm, "end": v(127.05, 28.38) * mm});
            skLineSegment(sketch, "E112.MirrorCS", {"start": v(94.05, 28.38) * mm, "end": v(94.05, -1.62) * mm, "construction": true});
            skLineSegment(sketch, "E113.MirrorCS", {"start": v(79.05, 10.38) * mm, "end": v(61.05, 28.38) * mm});
            skSolve(sketch);
        }
        {
            var Q0;
            Q0 = qSketchRegion(id + "F17", true);
            var Q1;
            Q1=makeQuery(id+"F2.opExtrude","CAP_FACE",FACE,{"disambiguationData":[OSD([sQuery(id+"F0.wireOp",EDGE,"E12"),sQuery(id+"F0.wireOp",EDGE,"E13"),sQuery(id+"F0.wireOp",EDGE,"E14"),sQuery(id+"F0.wireOp",EDGE,"E15"),sQuery(id+"F0.wireOp",EDGE,"E17.filletArc"),sQuery(id+"F0.wireOp",EDGE,"E18.filletArc"),sQuery(id+"F0.wireOp",EDGE,"E19.filletArc"),sQuery(id+"F0.wireOp",EDGE,"E20.filletArc"),sQuery(id+"F0.wireOp",EDGE,"E25.0"),sQuery(id+"F0.wireOp",EDGE,"E25.1"),sQuery(id+"F0.wireOp",EDGE,"E25.2"),sQuery(id+"F0.wireOp",EDGE,"E25.3"),sQuery(id+"F0.wireOp",EDGE,"E25.4"),sQuery(id+"F0.wireOp",EDGE,"E25.5"),sQuery(id+"F0.wireOp",EDGE,"E25.6"),sQuery(id+"F0.wireOp",EDGE,"E25.7")])],"isStart":false});
            extrude(context, id + "F18", {"entities" : qUnion([Q0]), "operationType" : NewBodyOperationType.ADD, "endBound" : BoundingType.UP_TO_SURFACE, "endBoundEntityFace" : qUnion([Q1]), "depth" : 25 * mm});
        }
    });
